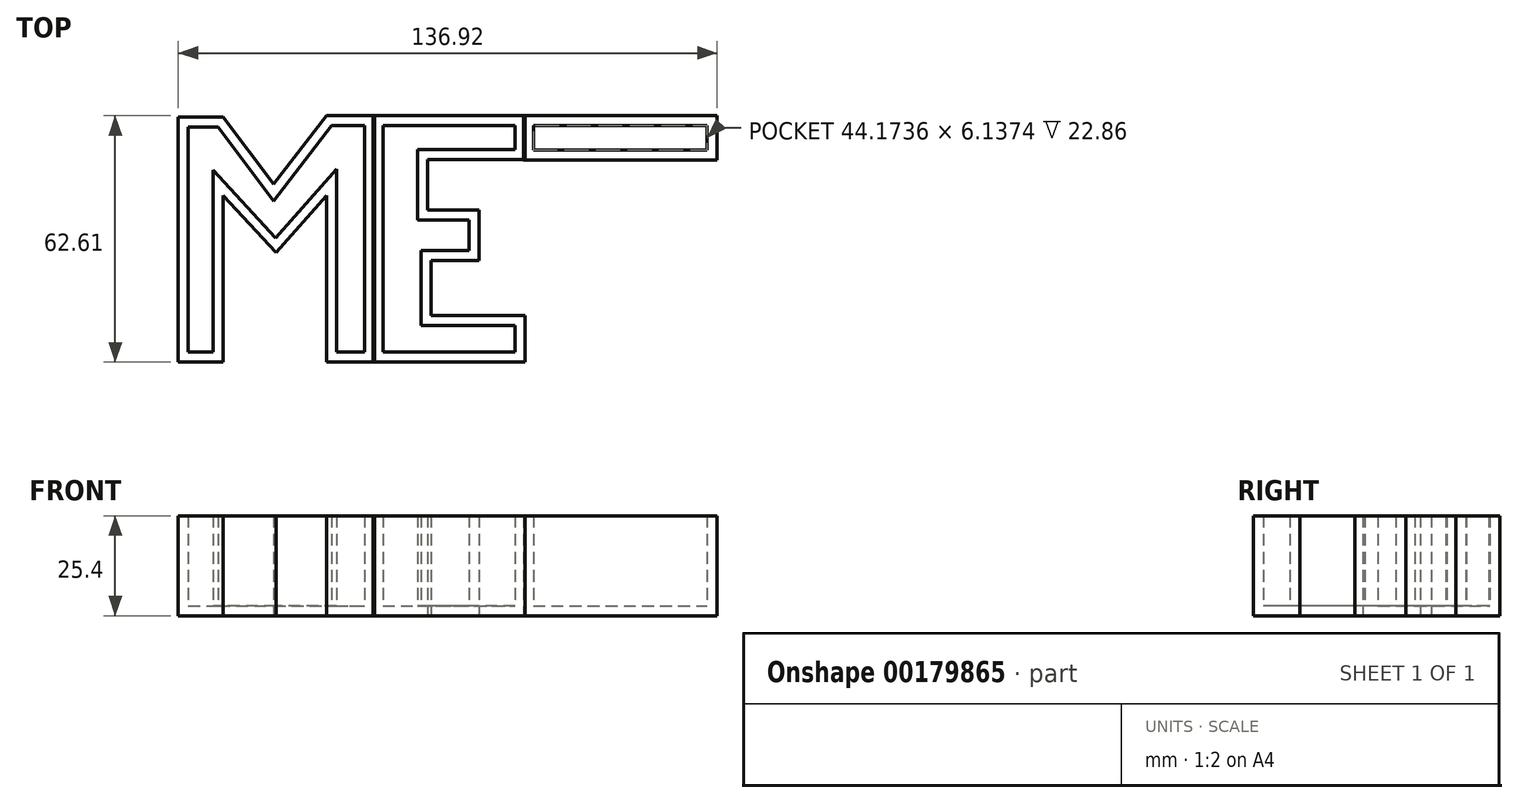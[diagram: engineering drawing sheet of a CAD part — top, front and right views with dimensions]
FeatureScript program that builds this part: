
annotation { "Feature Type Name" : "Feature", "Feature Type Description" : "" }
export const myFeature = defineFeature(function(context is Context, id is Id, definition is map)
    precondition{}
    {
        {
            var Q0;
            Q0=qCreatedBy(makeId("Top.planeOp"),FACE);
            var sketch = newSketch(context, id + "F0", { "sketchPlane" : qUnion([Q0])});
            skLineSegment(sketch, "E0.bottom", {"start": v(-69.6, 62.33) * mm, "end": v(-58.19, 62.33) * mm});
            skLineSegment(sketch, "E0.top", {"start": v(-69.6, 0) * mm, "end": v(-58.19, 0) * mm});
            skLineSegment(sketch, "E0.left", {"start": v(-69.6, 62.33) * mm, "end": v(-69.6, 0) * mm});
            skLineSegment(sketch, "E0.right", {"start": v(-58.19, 62.33) * mm, "end": v(-58.19, 0) * mm});
            skLineSegment(sketch, "E1.bottom", {"start": v(-31.95, 62.61) * mm, "end": v(-19.68, 62.61) * mm});
            skLineSegment(sketch, "E1.top", {"start": v(-31.95, 0) * mm, "end": v(-19.68, 0) * mm});
            skLineSegment(sketch, "E1.left", {"start": v(-31.95, 62.61) * mm, "end": v(-31.95, 0) * mm});
            skLineSegment(sketch, "E1.right", {"start": v(-19.68, 62.61) * mm, "end": v(-19.68, 0) * mm});
            skLineSegment(sketch, "E2", {"start": v(-58.19, 62.33) * mm, "end": v(-45.35, 45.21) * mm});
            skLineSegment(sketch, "E3", {"start": v(-45.35, 45.21) * mm, "end": v(-31.95, 62.61) * mm});
            skLineSegment(sketch, "E4", {"start": v(-31.95, 42.36) * mm, "end": v(-44.78, 27.81) * mm});
            skLineSegment(sketch, "E5", {"start": v(-44.78, 27.81) * mm, "end": v(-58.19, 42.36) * mm});
            skSolve(sketch);
        }
        {
            var Q0;
            Q0=qCreatedBy(makeId("Top.planeOp"),FACE);
            var sketch = newSketch(context, id + "F1", { "sketchPlane" : qUnion([Q0])});
            skLineSegment(sketch, "E6", {"start": v(-20.16, 62.61) * mm, "end": v(18.54, 62.61) * mm});
            skLineSegment(sketch, "E7", {"start": v(18.54, 62.61) * mm, "end": v(18.54, 51.49) * mm});
            skLineSegment(sketch, "E8", {"start": v(18.54, 51.49) * mm, "end": v(-6.28, 51.49) * mm});
            skLineSegment(sketch, "E9", {"start": v(-6.28, 51.49) * mm, "end": v(-6.28, 41.79) * mm});
            skLineSegment(sketch, "E10", {"start": v(-6.28, 41.79) * mm, "end": v(-6.28, 38.65) * mm});
            skLineSegment(sketch, "E11", {"start": v(-6.28, 38.65) * mm, "end": v(6.85, 38.65) * mm});
            skLineSegment(sketch, "E12", {"start": v(6.85, 38.65) * mm, "end": v(6.85, 25.81) * mm});
            skLineSegment(sketch, "E13", {"start": v(6.85, 25.81) * mm, "end": v(-5.42, 25.81) * mm});
            skLineSegment(sketch, "E14", {"start": v(-5.42, 25.81) * mm, "end": v(-5.42, 11.84) * mm});
            skLineSegment(sketch, "E15", {"start": v(-5.42, 11.84) * mm, "end": v(18.54, 11.84) * mm});
            skLineSegment(sketch, "E16", {"start": v(18.54, 11.84) * mm, "end": v(18.54, 0) * mm});
            skLineSegment(sketch, "E17", {"start": v(18.54, 0) * mm, "end": v(-20.16, 0) * mm});
            skLineSegment(sketch, "E18", {"start": v(-20.16, 0) * mm, "end": v(-20.16, 62.61) * mm});
            skSolve(sketch);
        }
        {
            var Q0;
            Q0=qCreatedBy(makeId("Top.planeOp"),FACE);
            var sketch = newSketch(context, id + "F2", { "sketchPlane" : qUnion([Q0])});
            skLineSegment(sketch, "E19.bottom", {"start": v(18.06, 62.61) * mm, "end": v(67.32, 62.61) * mm});
            skLineSegment(sketch, "E19.top", {"start": v(18.06, 51.4) * mm, "end": v(67.32, 51.4) * mm});
            skLineSegment(sketch, "E19.left", {"start": v(18.06, 62.61) * mm, "end": v(18.06, 51.4) * mm});
            skLineSegment(sketch, "E19.right", {"start": v(67.32, 62.61) * mm, "end": v(67.32, 51.4) * mm});
            skLineSegment(sketch, "E20.bottom", {"start": v(37.37, 51.4) * mm, "end": v(51.34, 51.4) * mm});
            skLineSegment(sketch, "E20.top", {"start": v(37.37, 0) * mm, "end": v(51.34, 0) * mm});
            skLineSegment(sketch, "E20.left", {"start": v(37.37, 51.4) * mm, "end": v(37.37, 0) * mm});
            skLineSegment(sketch, "E20.right", {"start": v(51.34, 51.4) * mm, "end": v(51.34, 0) * mm});
            skSolve(sketch);
        }
        {
            var Q0;
            {var subQ1=sQuery(id+"F0.wireOp",EDGE,"E2");Q0=makeQuery(id+"F0.imprint","IMPRINT",FACE,{"disambiguationData":[TD([[makeQuery(id+"F0.imprint","IMPRINT",EDGE,{"derivedFrom":subQ1}),-1.0]])]});}
            var Q1;
            {var subQ3=sQuery(id+"F0.wireOp",EDGE,"E1.bottom");Q1=makeQuery(id+"F0.imprint","IMPRINT",FACE,{"disambiguationData":[TD([[makeQuery(id+"F0.imprint","IMPRINT",EDGE,{"derivedFrom":subQ3}),-1.0]])]});}
            var Q2;
            Q2=makeQuery(id+"F1.imprint","IMPRINT",FACE,{"disambiguationData":[TD([[makeQuery(id+"F1.imprint","IMPRINT",EDGE,{"derivedFrom":sQuery(id+"F1.wireOp",EDGE,"E6")}),-1.0]])]});
            var Q3;
            {var subQ1=sQuery(id+"F0.wireOp",EDGE,"E0.bottom");Q3=makeQuery(id+"F0.imprint","IMPRINT",FACE,{"disambiguationData":[TD([[makeQuery(id+"F0.imprint","IMPRINT",EDGE,{"derivedFrom":subQ1}),-1.0]])]});}
            var Q4;
            Q4=makeQuery(id+"F2.imprint","IMPRINT",FACE,{"disambiguationData":[TD([[makeQuery(id+"F2.imprint","IMPRINT",EDGE,{"derivedFrom":sQuery(id+"F2.wireOp",EDGE,"E19.bottom")}),-1.0]])]});
            var Q5;
            Q5=makeQuery(id+"F2.imprint","IMPRINT",FACE,{"disambiguationData":[TD([[makeQuery(id+"F2.imprint","IMPRINT",EDGE,{"derivedFrom":sQuery(id+"F2.wireOp",EDGE,"E20.bottom")}),-1.0]])]});
            extrude(context, id + "F3", {"entities" : qUnion([Q0, Q1, Q2, Q3, Q4, Q5]), "depth" : 25.4 * mm});
        }
        {
            var Q0;
            Q0=makeQuery(id+"F3.opExtrude","CAP_FACE",FACE,{"disambiguationData":[OSD([sQuery(id+"F0.wireOp",EDGE,"E0.bottom"),sQuery(id+"F0.wireOp",EDGE,"E0.top"),sQuery(id+"F0.wireOp",EDGE,"E0.left"),sQuery(id+"F0.wireOp",EDGE,"E0.right"),sQuery(id+"F0.wireOp",EDGE,"E1.bottom"),sQuery(id+"F0.wireOp",EDGE,"E1.top"),sQuery(id+"F0.wireOp",EDGE,"E1.left"),sQuery(id+"F0.wireOp",EDGE,"E1.right"),sQuery(id+"F0.wireOp",EDGE,"E2"),sQuery(id+"F0.wireOp",EDGE,"E3"),sQuery(id+"F0.wireOp",EDGE,"E4"),sQuery(id+"F0.wireOp",EDGE,"E5")])],"isStart":false});
            var Q1;
            Q1=makeQuery(id+"F3.opExtrude","CAP_FACE",FACE,{"disambiguationData":[OSD([sQuery(id+"F1.wireOp",EDGE,"E6"),sQuery(id+"F1.wireOp",EDGE,"E7"),sQuery(id+"F1.wireOp",EDGE,"E8"),sQuery(id+"F1.wireOp",EDGE,"E9"),sQuery(id+"F1.wireOp",EDGE,"E10"),sQuery(id+"F1.wireOp",EDGE,"E11"),sQuery(id+"F1.wireOp",EDGE,"E12"),sQuery(id+"F1.wireOp",EDGE,"E13"),sQuery(id+"F1.wireOp",EDGE,"E14"),sQuery(id+"F1.wireOp",EDGE,"E15"),sQuery(id+"F1.wireOp",EDGE,"E16"),sQuery(id+"F1.wireOp",EDGE,"E17"),sQuery(id+"F1.wireOp",EDGE,"E18")])],"isStart":false});
            var Q2;
            Q2=makeQuery(id+"F3.opExtrude","CAP_FACE",FACE,{"disambiguationData":[OSD([sQuery(id+"F2.wireOp",EDGE,"E19.bottom"),sQuery(id+"F2.wireOp",EDGE,"E19.top"),sQuery(id+"F2.wireOp",EDGE,"E19.left"),sQuery(id+"F2.wireOp",EDGE,"E19.right"),sQuery(id+"F2.wireOp",EDGE,"E20.top"),sQuery(id+"F2.wireOp",EDGE,"E20.left"),sQuery(id+"F2.wireOp",EDGE,"E20.right")])],"isStart":false});
            shell(context, id + "F4", {"entities" : qUnion([Q0, Q1, Q2]), "thickness" : 2.54 * mm});
        }
    });
